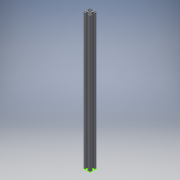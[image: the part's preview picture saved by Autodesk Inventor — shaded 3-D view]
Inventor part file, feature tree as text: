
AUTODESK INVENTOR PART (.ipt)
format: ipt  version: 2017 (Build 210142000, 142)  size: 356,352 bytes
history: native  units: mm
features: sketch x2, extrude x1, plane x1
ambient origin geometry x8: Origin, YZ Plane, XZ Plane, XY Plane, X Axis, Y Axis, Z Axis, Center Point
bodies: Solid1 (feature_tree)
feature tree (4):
  sketch  "Sketch1"  dims[d0=600.0mm d1=0.0mm]
  extrude  "Extrusion1"  [1 undecoded]
  plane  "Work Plane1"
  sketch  "Sketch3"
note: 1 required parameter value undecoded (feature->parameter linkage not recoverable at this tier; creation-order binding heuristic only, values carry confidence <= 0.55)
